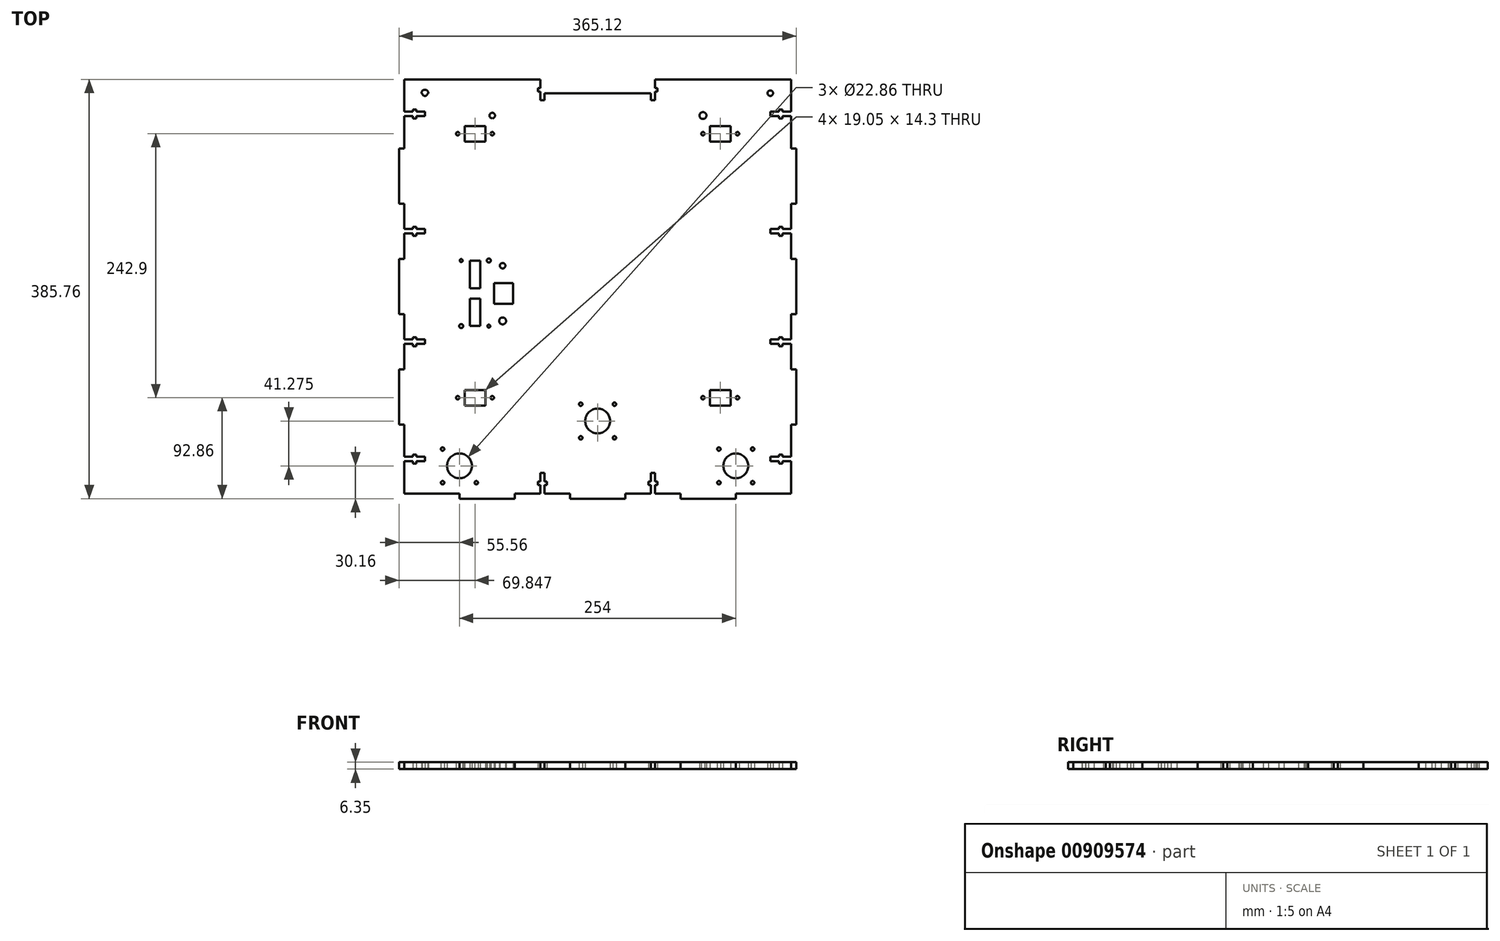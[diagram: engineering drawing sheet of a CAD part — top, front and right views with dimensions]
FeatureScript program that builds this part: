
annotation { "Feature Type Name" : "Feature", "Feature Type Description" : "" }
export const myFeature = defineFeature(function(context is Context, id is Id, definition is map)
    precondition{}
    {
        {
            var Q0;
            Q0=qCreatedBy(makeId("Top.planeOp"),FACE);
            var sketch = newSketch(context, id + "F0", { "sketchPlane" : qUnion([Q0])});
            skLineSegment(sketch, "E0.bottom", {"start": v(-177.8, 184.15) * mm, "end": v(177.8, 184.15) * mm});
            skLineSegment(sketch, "E0.top", {"start": v(-177.8, -184.15) * mm, "end": v(177.8, -184.15) * mm});
            skLineSegment(sketch, "E0.left", {"start": v(-177.8, 184.15) * mm, "end": v(-177.8, -184.15) * mm});
            skLineSegment(sketch, "E0.right", {"start": v(177.8, 184.15) * mm, "end": v(177.8, -184.15) * mm});
            skPoint(sketch, "E0.middle", {"position": v(0, 0) * mm});
            skLineSegment(sketch, "E1.0", {"start": v(-133.35, -88.9) * mm, "end": v(133.35, -88.9) * mm});
            skLineSegment(sketch, "E2.0", {"start": v(-133.35, 139.7) * mm, "end": v(-133.35, -88.9) * mm});
            skLineSegment(sketch, "E3", {"start": v(0, 184.15) * mm, "end": v(0, -184.15) * mm, "construction": true});
            skLineSegment(sketch, "E4", {"start": v(-177.8, 0) * mm, "end": v(177.8, 0) * mm, "construction": true});
            skLineSegment(sketch, "E5.MirrorCS", {"start": v(133.35, 139.7) * mm, "end": v(133.35, -88.9) * mm});
            skLineSegment(sketch, "E6.0", {"start": v(-133.35, 139.7) * mm, "end": v(133.35, 139.7) * mm});
            skLineSegment(sketch, "E7.bottom", {"start": v(-130.17, 34.93) * mm, "end": v(-95.25, 34.93) * mm});
            skLineSegment(sketch, "E7.top", {"start": v(-130.17, -34.92) * mm, "end": v(-95.25, -34.92) * mm});
            skLineSegment(sketch, "E7.left", {"start": v(-130.18, 34.92) * mm, "end": v(-130.18, -34.92) * mm});
            skLineSegment(sketch, "E7.right", {"start": v(-95.25, 34.92) * mm, "end": v(-95.25, -34.92) * mm});
            skLineSegment(sketch, "E8.bottom", {"start": v(-107.95, 4.76) * mm, "end": v(-117.48, 4.76) * mm});
            skLineSegment(sketch, "E8.top", {"start": v(-107.95, 30.04) * mm, "end": v(-117.48, 30.04) * mm});
            skLineSegment(sketch, "E8.left", {"start": v(-107.95, 4.76) * mm, "end": v(-107.95, 30.04) * mm});
            skLineSegment(sketch, "E8.right", {"start": v(-117.48, 4.76) * mm, "end": v(-117.48, 30.04) * mm});
            skPoint(sketch, "E9", {"position": v(-95.25, 0) * mm});
            skLineSegment(sketch, "E10.MirrorCS", {"start": v(-117.48, -4.76) * mm, "end": v(-117.48, -30.04) * mm});
            skLineSegment(sketch, "E11.MirrorCS", {"start": v(-107.95, -4.76) * mm, "end": v(-107.95, -30.04) * mm});
            skPoint(sketch, "E12.MirrorP", {"position": v(-112.71, -12.57) * mm});
            skLineSegment(sketch, "E13.MirrorCS", {"start": v(-107.95, -4.76) * mm, "end": v(-117.48, -4.76) * mm});
            skLineSegment(sketch, "E14.MirrorCS", {"start": v(-107.95, -30.04) * mm, "end": v(-117.48, -30.04) * mm});
            skCircle(sketch, "E15", {"center": v(-127, -158.75) * mm, "radius": 11.43 * mm});
            skCircle(sketch, "E16", {"center": v(-111.5, -143.26) * mm, "radius": 1.59 * mm});
            skCircle(sketch, "E17.1.0", {"center": v(-142.5, -143.26) * mm, "radius": 1.59 * mm});
            skCircle(sketch, "E17.2.0", {"center": v(-142.5, -174.24) * mm, "radius": 1.59 * mm});
            skCircle(sketch, "E17.3.0", {"center": v(-111.5, -174.24) * mm, "radius": 1.59 * mm});
            skCircle(sketch, "E18.MirrorC", {"center": v(142.5, -143.26) * mm, "radius": 1.59 * mm});
            skCircle(sketch, "E19.MirrorC", {"center": v(111.5, -143.26) * mm, "radius": 1.59 * mm});
            skCircle(sketch, "E20.MirrorC", {"center": v(142.5, -174.24) * mm, "radius": 1.59 * mm});
            skPoint(sketch, "E21.MirrorP", {"position": v(127, -158.75) * mm});
            skCircle(sketch, "E22.MirrorC", {"center": v(111.5, -174.24) * mm, "radius": 1.59 * mm});
            skCircle(sketch, "E23.MirrorC", {"center": v(127, -158.75) * mm, "radius": 11.43 * mm});
            skPoint(sketch, "E24.orphan", {"position": v(-112.71, -34.93) * mm});
            skCircle(sketch, "E25", {"center": v(-128.59, -96.05) * mm, "radius": 1.59 * mm});
            skCircle(sketch, "E26.MirrorC", {"center": v(-96.84, -96.05) * mm, "radius": 1.59 * mm});
            skLineSegment(sketch, "E27.bottom", {"start": v(-122.24, -88.9) * mm, "end": v(-103.19, -88.9) * mm});
            skLineSegment(sketch, "E27.top", {"start": v(-122.24, -103.2) * mm, "end": v(-103.19, -103.2) * mm});
            skLineSegment(sketch, "E27.left", {"start": v(-122.24, -88.9) * mm, "end": v(-122.24, -103.2) * mm});
            skLineSegment(sketch, "E27.right", {"start": v(-103.19, -88.9) * mm, "end": v(-103.19, -103.2) * mm});
            skPoint(sketch, "E28", {"position": v(-112.71, -103.2) * mm});
            skLineSegment(sketch, "E29.MirrorCS", {"start": v(122.24, -88.9) * mm, "end": v(122.24, -103.2) * mm});
            skCircle(sketch, "E30.MirrorC", {"center": v(96.84, -96.05) * mm, "radius": 1.59 * mm});
            skCircle(sketch, "E31.MirrorC", {"center": v(128.59, -96.05) * mm, "radius": 1.59 * mm});
            skLineSegment(sketch, "E32.MirrorCS", {"start": v(122.24, -88.9) * mm, "end": v(103.19, -88.9) * mm});
            skPoint(sketch, "E33.MirrorP", {"position": v(112.71, -103.2) * mm});
            skLineSegment(sketch, "E34.MirrorCS", {"start": v(103.19, -88.9) * mm, "end": v(103.19, -103.2) * mm});
            skLineSegment(sketch, "E35.MirrorCS", {"start": v(122.24, -103.2) * mm, "end": v(103.19, -103.2) * mm});
            skLineSegment(sketch, "E36.bottom", {"start": v(-95.25, -9.53) * mm, "end": v(-77.79, -9.53) * mm});
            skLineSegment(sketch, "E36.top", {"start": v(-95.25, 9.52) * mm, "end": v(-77.79, 9.52) * mm});
            skLineSegment(sketch, "E36.left", {"start": v(-95.25, -9.53) * mm, "end": v(-95.25, 9.52) * mm});
            skLineSegment(sketch, "E36.right", {"start": v(-77.79, -9.53) * mm, "end": v(-77.79, 9.52) * mm});
            skPoint(sketch, "E37", {"position": v(-65.09, 0) * mm});
            skLineSegment(sketch, "E38.bottom", {"start": v(-95.25, -34.92) * mm, "end": v(-77.79, -34.92) * mm});
            skLineSegment(sketch, "E38.top", {"start": v(-95.25, 34.93) * mm, "end": v(-77.79, 34.93) * mm});
            skLineSegment(sketch, "E38.left", {"start": v(-95.25, -34.92) * mm, "end": v(-95.25, 34.92) * mm});
            skLineSegment(sketch, "E38.right", {"start": v(-77.79, -34.92) * mm, "end": v(-77.79, 34.92) * mm});
            skLineSegment(sketch, "E39.0", {"start": v(-100.01, 34.92) * mm, "end": v(-77.79, 34.92) * mm});
            skLineSegment(sketch, "E39.1", {"start": v(-130.18, 34.92) * mm, "end": v(-100.01, 34.92) * mm});
            skLineSegment(sketch, "E40", {"start": v(-77.79, 34.92) * mm, "end": v(-77.79, 34.92) * mm});
            skLineSegment(sketch, "E41", {"start": v(-130.18, 34.92) * mm, "end": v(-130.18, 34.92) * mm});
            skLineSegment(sketch, "E42.MirrorCS", {"start": v(-130.18, -34.92) * mm, "end": v(-130.18, -34.92) * mm});
            skLineSegment(sketch, "E43.MirrorCS", {"start": v(-100.01, -34.93) * mm, "end": v(-77.79, -34.93) * mm});
            skLineSegment(sketch, "E44.MirrorCS", {"start": v(-130.18, -34.93) * mm, "end": v(-100.01, -34.93) * mm});
            skLineSegment(sketch, "E45.MirrorCS", {"start": v(-77.79, -34.92) * mm, "end": v(-77.79, -34.92) * mm});
            skCircle(sketch, "E46", {"center": v(-87.31, 25.4) * mm, "radius": 3.18 * mm});
            skCircle(sketch, "E47.MirrorC", {"center": v(-87.31, -25.4) * mm, "radius": 3.18 * mm});
            skCircle(sketch, "E48", {"center": v(-125.41, 30.16) * mm, "radius": 1.84 * mm});
            skCircle(sketch, "E49.MirrorC", {"center": v(-100.01, 30.16) * mm, "radius": 1.84 * mm});
            skCircle(sketch, "E50.MirrorC", {"center": v(-125.41, -30.16) * mm, "radius": 1.84 * mm});
            skCircle(sketch, "E51.MirrorC", {"center": v(-100.01, -30.16) * mm, "radius": 1.84 * mm});
            skCircle(sketch, "E52", {"center": v(-158.75, 184.15) * mm, "radius": 3.18 * mm});
            skCircle(sketch, "E53", {"center": v(-96.84, 163.55) * mm, "radius": 3.18 * mm});
            skCircle(sketch, "E54.MirrorC", {"center": v(158.75, 184.15) * mm, "radius": 3.18 * mm});
            skLineSegment(sketch, "E55.0", {"start": v(-177.8, 196.85) * mm, "end": v(177.8, 196.85) * mm});
            skLineSegment(sketch, "E56", {"start": v(-177.8, 184.15) * mm, "end": v(-177.8, 196.85) * mm});
            skLineSegment(sketch, "E57", {"start": v(177.8, 184.15) * mm, "end": v(177.8, 196.85) * mm});
            skLineSegment(sketch, "E58.bottom", {"start": v(-177.8, 133.35) * mm, "end": v(-182.56, 133.35) * mm});
            skLineSegment(sketch, "E58.top", {"start": v(-177.8, 82.55) * mm, "end": v(-182.56, 82.55) * mm});
            skLineSegment(sketch, "E58.left", {"start": v(-177.8, 133.35) * mm, "end": v(-177.8, 82.55) * mm});
            skLineSegment(sketch, "E58.right", {"start": v(-182.56, 133.35) * mm, "end": v(-182.56, 82.55) * mm});
            skLineSegment(sketch, "E59.bottom", {"start": v(-177.8, 31.75) * mm, "end": v(-182.56, 31.75) * mm});
            skLineSegment(sketch, "E59.top", {"start": v(-177.8, -19.05) * mm, "end": v(-182.56, -19.05) * mm});
            skLineSegment(sketch, "E59.left", {"start": v(-177.8, 31.75) * mm, "end": v(-177.8, -19.05) * mm});
            skLineSegment(sketch, "E59.right", {"start": v(-182.56, 31.75) * mm, "end": v(-182.56, -19.05) * mm});
            skLineSegment(sketch, "E60.bottom", {"start": v(-177.8, -69.85) * mm, "end": v(-182.56, -69.85) * mm});
            skLineSegment(sketch, "E60.top", {"start": v(-177.8, -120.65) * mm, "end": v(-182.56, -120.65) * mm});
            skLineSegment(sketch, "E60.left", {"start": v(-177.8, -69.85) * mm, "end": v(-177.8, -120.65) * mm});
            skLineSegment(sketch, "E60.right", {"start": v(-182.56, -69.85) * mm, "end": v(-182.56, -120.65) * mm});
            skLineSegment(sketch, "E61.MirrorCS", {"start": v(177.8, -120.65) * mm, "end": v(182.56, -120.65) * mm});
            skLineSegment(sketch, "E62.MirrorCS", {"start": v(177.8, 31.75) * mm, "end": v(182.56, 31.75) * mm});
            skLineSegment(sketch, "E63.MirrorCS", {"start": v(177.8, -19.05) * mm, "end": v(182.56, -19.05) * mm});
            skLineSegment(sketch, "E64.MirrorCS", {"start": v(177.8, 82.55) * mm, "end": v(182.56, 82.55) * mm});
            skLineSegment(sketch, "E65.MirrorCS", {"start": v(177.8, -69.85) * mm, "end": v(182.56, -69.85) * mm});
            skLineSegment(sketch, "E66.MirrorCS", {"start": v(177.8, 133.35) * mm, "end": v(182.56, 133.35) * mm});
            skLineSegment(sketch, "E67.MirrorCS", {"start": v(182.56, 133.35) * mm, "end": v(182.56, 82.55) * mm});
            skLineSegment(sketch, "E68.MirrorCS", {"start": v(177.8, 31.75) * mm, "end": v(177.8, -19.05) * mm});
            skLineSegment(sketch, "E69.MirrorCS", {"start": v(182.56, 31.75) * mm, "end": v(182.56, -19.05) * mm});
            skLineSegment(sketch, "E70.MirrorCS", {"start": v(177.8, 133.35) * mm, "end": v(177.8, 82.55) * mm});
            skLineSegment(sketch, "E71.MirrorCS", {"start": v(177.8, -69.85) * mm, "end": v(177.8, -120.65) * mm});
            skLineSegment(sketch, "E72.MirrorCS", {"start": v(182.56, -69.85) * mm, "end": v(182.56, -120.65) * mm});
            skLineSegment(sketch, "E73.bottom", {"start": v(-127, 196.85) * mm, "end": v(-76.2, 196.85) * mm});
            skLineSegment(sketch, "E73.top", {"start": v(-127, 201.61) * mm, "end": v(-76.2, 201.61) * mm});
            skLineSegment(sketch, "E73.left", {"start": v(-127, 196.85) * mm, "end": v(-127, 201.61) * mm});
            skLineSegment(sketch, "E73.right", {"start": v(-76.2, 196.85) * mm, "end": v(-76.2, 201.61) * mm});
            skLineSegment(sketch, "E74.bottom", {"start": v(-25.4, 196.85) * mm, "end": v(25.4, 196.85) * mm});
            skLineSegment(sketch, "E74.top", {"start": v(-25.4, 201.61) * mm, "end": v(25.4, 201.61) * mm});
            skLineSegment(sketch, "E74.left", {"start": v(-25.4, 196.85) * mm, "end": v(-25.4, 201.61) * mm});
            skLineSegment(sketch, "E74.right", {"start": v(25.4, 196.85) * mm, "end": v(25.4, 201.61) * mm});
            skLineSegment(sketch, "E75.bottom", {"start": v(76.2, 196.85) * mm, "end": v(127, 196.85) * mm});
            skLineSegment(sketch, "E75.top", {"start": v(76.2, 201.61) * mm, "end": v(127, 201.61) * mm});
            skLineSegment(sketch, "E75.left", {"start": v(76.2, 196.85) * mm, "end": v(76.2, 201.61) * mm});
            skLineSegment(sketch, "E75.right", {"start": v(127, 196.85) * mm, "end": v(127, 201.61) * mm});
            skLineSegment(sketch, "E76", {"start": v(177.8, 196.85) * mm, "end": v(177.8, -184.15) * mm, "construction": true});
            skLineSegment(sketch, "E77", {"start": v(177.8, 6.35) * mm, "end": v(-210.69, 6.35) * mm, "construction": true});
            skLineSegment(sketch, "E78.MirrorCS", {"start": v(25.4, -184.15) * mm, "end": v(25.4, -188.91) * mm});
            skLineSegment(sketch, "E79.MirrorCS", {"start": v(76.2, -184.15) * mm, "end": v(76.2, -188.91) * mm});
            skLineSegment(sketch, "E80.MirrorCS", {"start": v(127, -184.15) * mm, "end": v(127, -188.91) * mm});
            skLineSegment(sketch, "E81.MirrorCS", {"start": v(-127, -184.15) * mm, "end": v(-127, -188.91) * mm});
            skLineSegment(sketch, "E82.MirrorCS", {"start": v(-25.4, -184.15) * mm, "end": v(-25.4, -188.91) * mm});
            skLineSegment(sketch, "E83.MirrorCS", {"start": v(-76.2, -184.15) * mm, "end": v(-76.2, -188.91) * mm});
            skLineSegment(sketch, "E84.MirrorCS", {"start": v(76.2, -184.15) * mm, "end": v(127, -184.15) * mm});
            skLineSegment(sketch, "E85.MirrorCS", {"start": v(-127, -188.91) * mm, "end": v(-76.2, -188.91) * mm});
            skLineSegment(sketch, "E86.MirrorCS", {"start": v(76.2, -188.91) * mm, "end": v(127, -188.91) * mm});
            skLineSegment(sketch, "E87.MirrorCS", {"start": v(-25.4, -184.15) * mm, "end": v(25.4, -184.15) * mm});
            skLineSegment(sketch, "E88.MirrorCS", {"start": v(-25.4, -188.91) * mm, "end": v(25.4, -188.91) * mm});
            skLineSegment(sketch, "E89.MirrorCS", {"start": v(-127, -184.15) * mm, "end": v(-76.2, -184.15) * mm});
            skCircle(sketch, "E90", {"center": v(0, -117.47) * mm, "radius": 11.43 * mm});
            skLineSegment(sketch, "E91.bottom", {"start": v(20.64, -96.84) * mm, "end": v(-20.64, -96.84) * mm});
            skLineSegment(sketch, "E91.top", {"start": v(20.64, -138.11) * mm, "end": v(-20.64, -138.11) * mm});
            skLineSegment(sketch, "E91.left", {"start": v(20.64, -96.84) * mm, "end": v(20.64, -138.11) * mm});
            skLineSegment(sketch, "E91.right", {"start": v(-20.64, -96.84) * mm, "end": v(-20.64, -138.11) * mm});
            skCircle(sketch, "E92", {"center": v(-15.5, -132.97) * mm, "radius": 1.59 * mm});
            skCircle(sketch, "E93.1.0", {"center": v(15.5, -132.97) * mm, "radius": 1.59 * mm});
            skCircle(sketch, "E93.2.0", {"center": v(15.5, -101.98) * mm, "radius": 1.59 * mm});
            skCircle(sketch, "E94.1.3.0", {"center": v(-15.5, -101.98) * mm, "radius": 1.59 * mm});
            skPoint(sketch, "E95.orphan", {"position": v(-112.71, 34.93) * mm});
            skLineSegment(sketch, "E96", {"start": v(133.35, 25.4) * mm, "end": v(-130.18, 25.4) * mm, "construction": true});
            skCircle(sketch, "E97.MirrorC", {"center": v(-128.59, 146.85) * mm, "radius": 1.59 * mm});
            skLineSegment(sketch, "E98.MirrorCS", {"start": v(-122.24, 154) * mm, "end": v(-103.19, 154) * mm});
            skCircle(sketch, "E99.MirrorC", {"center": v(-96.84, 146.85) * mm, "radius": 1.59 * mm});
            skLineSegment(sketch, "E100.MirrorCS", {"start": v(-122.24, 139.7) * mm, "end": v(-103.19, 139.7) * mm});
            skLineSegment(sketch, "E101.MirrorCS", {"start": v(-122.24, 139.7) * mm, "end": v(-122.24, 154) * mm});
            skLineSegment(sketch, "E102.MirrorCS", {"start": v(-103.19, 139.7) * mm, "end": v(-103.19, 154) * mm});
            skPoint(sketch, "E103.MirrorP", {"position": v(-112.71, 154) * mm});
            skCircle(sketch, "E104.MirrorC", {"center": v(96.84, 146.85) * mm, "radius": 1.59 * mm});
            skLineSegment(sketch, "E105.MirrorCS", {"start": v(122.24, 154) * mm, "end": v(103.19, 154) * mm});
            skCircle(sketch, "E106.MirrorC", {"center": v(128.59, 146.85) * mm, "radius": 1.59 * mm});
            skLineSegment(sketch, "E107.MirrorCS", {"start": v(122.24, 139.7) * mm, "end": v(103.19, 139.7) * mm});
            skLineSegment(sketch, "E108.MirrorCS", {"start": v(103.19, 139.7) * mm, "end": v(103.19, 154) * mm});
            skPoint(sketch, "E109.MirrorP", {"position": v(112.71, 154) * mm});
            skLineSegment(sketch, "E110.MirrorCS", {"start": v(122.24, 139.7) * mm, "end": v(122.24, 154) * mm});
            skCircle(sketch, "E111.MirrorC", {"center": v(96.84, 163.55) * mm, "radius": 3.18 * mm});
            skLineSegment(sketch, "E112.bottom", {"start": v(-158.75, -150.4) * mm, "end": v(-158.75, -154.4) * mm});
            skLineSegment(sketch, "E112.top", {"start": v(-177.8, -150.4) * mm, "end": v(-177.8, -154.4) * mm});
            skLineSegment(sketch, "E112.left", {"start": v(-158.75, -150.4) * mm, "end": v(-177.8, -150.4) * mm});
            skLineSegment(sketch, "E112.right", {"start": v(-158.75, -154.4) * mm, "end": v(-177.8, -154.4) * mm});
            skPoint(sketch, "E113", {"position": v(-177.8, -152.4) * mm});
            skLineSegment(sketch, "E114.bottom", {"start": v(-166.67, -148.27) * mm, "end": v(-166.67, -156.53) * mm});
            skLineSegment(sketch, "E114.top", {"start": v(-169.85, -148.27) * mm, "end": v(-169.85, -156.53) * mm});
            skLineSegment(sketch, "E114.left", {"start": v(-166.67, -148.27) * mm, "end": v(-169.85, -148.27) * mm});
            skLineSegment(sketch, "E114.right", {"start": v(-166.67, -156.53) * mm, "end": v(-169.85, -156.53) * mm});
            skPoint(sketch, "E115", {"position": v(-169.85, -152.4) * mm});
            skLineSegment(sketch, "E116", {"start": v(-177.8, -19.05) * mm, "end": v(-177.8, -69.85) * mm, "construction": true});
            skLineSegment(sketch, "E117", {"start": v(-177.8, -120.65) * mm, "end": v(-177.8, -184.15) * mm, "construction": true});
            skLineSegment(sketch, "E118", {"start": v(-177.8, 31.75) * mm, "end": v(-177.8, 82.55) * mm, "construction": true});
            skLineSegment(sketch, "E119", {"start": v(-177.8, 133.35) * mm, "end": v(-177.8, 196.85) * mm, "construction": true});
            skPoint(sketch, "E120", {"position": v(-177.8, 165.1) * mm});
            skPoint(sketch, "E121", {"position": v(-177.8, 57.15) * mm});
            skPoint(sketch, "E122", {"position": v(-177.8, -44.45) * mm});
            skLineSegment(sketch, "E123.bottom", {"start": v(-158.75, -42.46) * mm, "end": v(-158.75, -46.44) * mm});
            skLineSegment(sketch, "E123.top", {"start": v(-177.8, -42.46) * mm, "end": v(-177.8, -46.44) * mm});
            skLineSegment(sketch, "E123.left", {"start": v(-158.75, -42.46) * mm, "end": v(-177.8, -42.46) * mm});
            skLineSegment(sketch, "E123.right", {"start": v(-158.75, -46.44) * mm, "end": v(-177.8, -46.44) * mm});
            skLineSegment(sketch, "E124.bottom", {"start": v(-166.67, -40.32) * mm, "end": v(-166.67, -48.58) * mm});
            skLineSegment(sketch, "E124.top", {"start": v(-169.85, -40.32) * mm, "end": v(-169.85, -48.58) * mm});
            skLineSegment(sketch, "E124.left", {"start": v(-166.67, -40.32) * mm, "end": v(-169.85, -40.32) * mm});
            skLineSegment(sketch, "E124.right", {"start": v(-166.67, -48.58) * mm, "end": v(-169.85, -48.58) * mm});
            skPoint(sketch, "E125", {"position": v(-169.85, -44.45) * mm});
            skLineSegment(sketch, "E126.bottom", {"start": v(-158.75, 59.14) * mm, "end": v(-158.75, 55.16) * mm});
            skLineSegment(sketch, "E126.top", {"start": v(-177.8, 59.14) * mm, "end": v(-177.8, 55.16) * mm});
            skLineSegment(sketch, "E126.left", {"start": v(-158.75, 59.14) * mm, "end": v(-177.8, 59.14) * mm});
            skLineSegment(sketch, "E126.right", {"start": v(-158.75, 55.16) * mm, "end": v(-177.8, 55.16) * mm});
            skLineSegment(sketch, "E127.bottom", {"start": v(-166.67, 61.28) * mm, "end": v(-166.67, 53.02) * mm});
            skLineSegment(sketch, "E127.top", {"start": v(-169.85, 61.28) * mm, "end": v(-169.85, 53.02) * mm});
            skLineSegment(sketch, "E127.left", {"start": v(-166.67, 61.28) * mm, "end": v(-169.85, 61.28) * mm});
            skLineSegment(sketch, "E127.right", {"start": v(-166.67, 53.02) * mm, "end": v(-169.85, 53.02) * mm});
            skPoint(sketch, "E128", {"position": v(-169.85, 57.15) * mm});
            skLineSegment(sketch, "E129.bottom", {"start": v(-158.75, 167.1) * mm, "end": v(-158.75, 163.1) * mm});
            skLineSegment(sketch, "E129.top", {"start": v(-177.8, 167.1) * mm, "end": v(-177.8, 163.1) * mm});
            skLineSegment(sketch, "E129.left", {"start": v(-158.75, 167.1) * mm, "end": v(-177.8, 167.1) * mm});
            skLineSegment(sketch, "E129.right", {"start": v(-158.75, 163.1) * mm, "end": v(-177.8, 163.1) * mm});
            skLineSegment(sketch, "E130.bottom", {"start": v(-166.67, 169.23) * mm, "end": v(-166.67, 160.97) * mm});
            skLineSegment(sketch, "E130.top", {"start": v(-169.85, 169.23) * mm, "end": v(-169.85, 160.97) * mm});
            skLineSegment(sketch, "E130.left", {"start": v(-166.67, 169.23) * mm, "end": v(-169.85, 169.23) * mm});
            skLineSegment(sketch, "E130.right", {"start": v(-166.67, 160.97) * mm, "end": v(-169.85, 160.97) * mm});
            skPoint(sketch, "E131", {"position": v(-169.85, 165.1) * mm});
            skLineSegment(sketch, "E132.MirrorCS", {"start": v(177.8, 167.1) * mm, "end": v(177.8, 163.1) * mm});
            skLineSegment(sketch, "E133.MirrorCS", {"start": v(166.67, 169.23) * mm, "end": v(169.85, 169.23) * mm});
            skPoint(sketch, "E134.MirrorP", {"position": v(177.8, 165.1) * mm});
            skLineSegment(sketch, "E135.MirrorCS", {"start": v(158.75, 163.1) * mm, "end": v(177.8, 163.1) * mm});
            skLineSegment(sketch, "E136.MirrorCS", {"start": v(169.85, 169.23) * mm, "end": v(169.85, 160.97) * mm});
            skPoint(sketch, "E137.MirrorP", {"position": v(169.85, 165.1) * mm});
            skLineSegment(sketch, "E138.MirrorCS", {"start": v(166.67, 169.23) * mm, "end": v(166.67, 160.97) * mm});
            skLineSegment(sketch, "E139.MirrorCS", {"start": v(158.75, 167.1) * mm, "end": v(158.75, 163.1) * mm});
            skLineSegment(sketch, "E140.MirrorCS", {"start": v(158.75, 167.1) * mm, "end": v(177.8, 167.1) * mm});
            skLineSegment(sketch, "E141.MirrorCS", {"start": v(166.67, 160.97) * mm, "end": v(169.85, 160.97) * mm});
            skLineSegment(sketch, "E142.MirrorCS", {"start": v(177.8, 59.14) * mm, "end": v(177.8, 55.16) * mm});
            skLineSegment(sketch, "E143.MirrorCS", {"start": v(166.67, 61.28) * mm, "end": v(169.85, 61.28) * mm});
            skPoint(sketch, "E144.MirrorP", {"position": v(177.8, 57.15) * mm});
            skLineSegment(sketch, "E145.MirrorCS", {"start": v(158.75, 59.14) * mm, "end": v(177.8, 59.14) * mm});
            skLineSegment(sketch, "E146.MirrorCS", {"start": v(166.67, 61.28) * mm, "end": v(166.67, 53.02) * mm});
            skLineSegment(sketch, "E147.MirrorCS", {"start": v(169.85, 61.28) * mm, "end": v(169.85, 53.02) * mm});
            skLineSegment(sketch, "E148.MirrorCS", {"start": v(166.67, 53.02) * mm, "end": v(169.85, 53.02) * mm});
            skPoint(sketch, "E149.MirrorP", {"position": v(169.85, 57.15) * mm});
            skLineSegment(sketch, "E150.MirrorCS", {"start": v(158.75, 55.16) * mm, "end": v(177.8, 55.16) * mm});
            skLineSegment(sketch, "E151.MirrorCS", {"start": v(158.75, 59.14) * mm, "end": v(158.75, 55.16) * mm});
            skLineSegment(sketch, "E152.MirrorCS", {"start": v(177.8, -42.46) * mm, "end": v(177.8, -46.44) * mm});
            skLineSegment(sketch, "E153.MirrorCS", {"start": v(166.67, -40.32) * mm, "end": v(169.85, -40.32) * mm});
            skPoint(sketch, "E154.MirrorP", {"position": v(177.8, -44.45) * mm});
            skLineSegment(sketch, "E155.MirrorCS", {"start": v(169.85, -40.32) * mm, "end": v(169.85, -48.58) * mm});
            skPoint(sketch, "E156.MirrorP", {"position": v(169.85, -44.45) * mm});
            skLineSegment(sketch, "E157.MirrorCS", {"start": v(158.75, -42.46) * mm, "end": v(158.75, -46.44) * mm});
            skLineSegment(sketch, "E158.MirrorCS", {"start": v(166.67, -40.32) * mm, "end": v(166.67, -48.58) * mm});
            skLineSegment(sketch, "E159.MirrorCS", {"start": v(166.67, -48.58) * mm, "end": v(169.85, -48.58) * mm});
            skLineSegment(sketch, "E160.MirrorCS", {"start": v(158.75, -42.46) * mm, "end": v(177.8, -42.46) * mm});
            skLineSegment(sketch, "E161.MirrorCS", {"start": v(158.75, -46.44) * mm, "end": v(177.8, -46.44) * mm});
            skLineSegment(sketch, "E162.MirrorCS", {"start": v(177.8, -150.4) * mm, "end": v(177.8, -154.4) * mm});
            skLineSegment(sketch, "E163.MirrorCS", {"start": v(166.67, -148.27) * mm, "end": v(169.85, -148.27) * mm});
            skPoint(sketch, "E164.MirrorP", {"position": v(177.8, -152.4) * mm});
            skLineSegment(sketch, "E165.MirrorCS", {"start": v(158.75, -150.4) * mm, "end": v(158.75, -154.4) * mm});
            skLineSegment(sketch, "E166.MirrorCS", {"start": v(166.67, -148.27) * mm, "end": v(166.67, -156.53) * mm});
            skLineSegment(sketch, "E167.MirrorCS", {"start": v(166.67, -156.53) * mm, "end": v(169.85, -156.53) * mm});
            skLineSegment(sketch, "E168.MirrorCS", {"start": v(158.75, -150.4) * mm, "end": v(177.8, -150.4) * mm});
            skLineSegment(sketch, "E169.MirrorCS", {"start": v(169.85, -148.27) * mm, "end": v(169.85, -156.53) * mm});
            skPoint(sketch, "E170.MirrorP", {"position": v(169.85, -152.4) * mm});
            skLineSegment(sketch, "E171.MirrorCS", {"start": v(158.75, -154.4) * mm, "end": v(177.8, -154.4) * mm});
            skLineSegment(sketch, "E172", {"start": v(-76.2, 196.85) * mm, "end": v(-25.4, 196.85) * mm, "construction": true});
            skLineSegment(sketch, "E173", {"start": v(25.4, 196.85) * mm, "end": v(76.2, 196.85) * mm, "construction": true});
            skLineSegment(sketch, "E174", {"start": v(-76.2, -184.15) * mm, "end": v(-25.4, -184.15) * mm, "construction": true});
            skLineSegment(sketch, "E175", {"start": v(25.4, -184.15) * mm, "end": v(76.2, -184.15) * mm, "construction": true});
            skLineSegment(sketch, "E176.bottom", {"start": v(-48.8, 177.8) * mm, "end": v(-52.8, 177.8) * mm});
            skLineSegment(sketch, "E176.top", {"start": v(-48.8, 196.85) * mm, "end": v(-52.8, 196.85) * mm});
            skLineSegment(sketch, "E176.left", {"start": v(-48.8, 177.8) * mm, "end": v(-48.8, 196.85) * mm});
            skLineSegment(sketch, "E176.right", {"start": v(-52.8, 177.8) * mm, "end": v(-52.8, 196.85) * mm});
            skPoint(sketch, "E177", {"position": v(-50.8, 196.85) * mm});
            skLineSegment(sketch, "E178.bottom", {"start": v(-46.67, 185.72) * mm, "end": v(-54.93, 185.72) * mm});
            skLineSegment(sketch, "E178.top", {"start": v(-46.67, 188.9) * mm, "end": v(-54.93, 188.9) * mm});
            skLineSegment(sketch, "E178.left", {"start": v(-46.67, 185.72) * mm, "end": v(-46.67, 188.9) * mm});
            skLineSegment(sketch, "E178.right", {"start": v(-54.93, 185.72) * mm, "end": v(-54.93, 188.9) * mm});
            skPoint(sketch, "E179", {"position": v(-50.8, 188.9) * mm});
            skPoint(sketch, "E180", {"position": v(50.8, 196.85) * mm});
            skLineSegment(sketch, "E181.bottom", {"start": v(52.8, 177.8) * mm, "end": v(48.8, 177.8) * mm});
            skLineSegment(sketch, "E181.top", {"start": v(52.8, 196.85) * mm, "end": v(48.8, 196.85) * mm});
            skLineSegment(sketch, "E181.left", {"start": v(52.8, 177.8) * mm, "end": v(52.8, 196.85) * mm});
            skLineSegment(sketch, "E181.right", {"start": v(48.8, 177.8) * mm, "end": v(48.8, 196.85) * mm});
            skLineSegment(sketch, "E182.bottom", {"start": v(54.93, 185.72) * mm, "end": v(46.67, 185.72) * mm});
            skLineSegment(sketch, "E182.top", {"start": v(54.93, 188.9) * mm, "end": v(46.67, 188.9) * mm});
            skLineSegment(sketch, "E182.left", {"start": v(54.93, 185.72) * mm, "end": v(54.93, 188.9) * mm});
            skLineSegment(sketch, "E182.right", {"start": v(46.67, 185.72) * mm, "end": v(46.67, 188.9) * mm});
            skPoint(sketch, "E183", {"position": v(50.8, 188.9) * mm});
            skLineSegment(sketch, "E184.MirrorCS", {"start": v(-46.67, -173.02) * mm, "end": v(-46.67, -176.2) * mm});
            skLineSegment(sketch, "E185.MirrorCS", {"start": v(-48.8, -165.1) * mm, "end": v(-52.8, -165.1) * mm});
            skLineSegment(sketch, "E186.MirrorCS", {"start": v(-48.8, -184.15) * mm, "end": v(-52.8, -184.15) * mm});
            skLineSegment(sketch, "E187.MirrorCS", {"start": v(-54.93, -173.02) * mm, "end": v(-54.93, -176.2) * mm});
            skLineSegment(sketch, "E188.MirrorCS", {"start": v(-46.67, -173.02) * mm, "end": v(-54.93, -173.02) * mm});
            skLineSegment(sketch, "E189.MirrorCS", {"start": v(-46.67, -176.2) * mm, "end": v(-54.93, -176.2) * mm});
            skPoint(sketch, "E190.MirrorP", {"position": v(-50.8, -184.15) * mm});
            skLineSegment(sketch, "E191.MirrorCS", {"start": v(-48.8, -165.1) * mm, "end": v(-48.8, -184.15) * mm});
            skLineSegment(sketch, "E192.MirrorCS", {"start": v(-52.8, -165.1) * mm, "end": v(-52.8, -184.15) * mm});
            skPoint(sketch, "E193.MirrorP", {"position": v(-50.8, -176.2) * mm});
            skLineSegment(sketch, "E194.MirrorCS", {"start": v(54.93, -173.02) * mm, "end": v(54.93, -176.2) * mm});
            skLineSegment(sketch, "E195.MirrorCS", {"start": v(52.8, -184.15) * mm, "end": v(48.8, -184.15) * mm});
            skLineSegment(sketch, "E196.MirrorCS", {"start": v(46.67, -173.02) * mm, "end": v(46.67, -176.2) * mm});
            skLineSegment(sketch, "E197.MirrorCS", {"start": v(52.8, -165.1) * mm, "end": v(48.8, -165.1) * mm});
            skPoint(sketch, "E198.MirrorP", {"position": v(50.8, -184.15) * mm});
            skLineSegment(sketch, "E199.MirrorCS", {"start": v(54.93, -176.2) * mm, "end": v(46.67, -176.2) * mm});
            skLineSegment(sketch, "E200.MirrorCS", {"start": v(52.8, -165.1) * mm, "end": v(52.8, -184.15) * mm});
            skPoint(sketch, "E201.MirrorP", {"position": v(50.8, -176.2) * mm});
            skLineSegment(sketch, "E202.MirrorCS", {"start": v(48.8, -165.1) * mm, "end": v(48.8, -184.15) * mm});
            skLineSegment(sketch, "E203.MirrorCS", {"start": v(54.93, -173.02) * mm, "end": v(46.67, -173.02) * mm});
            skSolve(sketch);
        }
        {
            var Q0;
            Q0=makeQuery(id+"F0.imprint","IMPRINT",FACE,{"disambiguationData":[TD([[makeQuery(id+"F0.imprint","IMPRINT",EDGE,{"derivedFrom":sQuery(id+"F0.wireOp",EDGE,"E0.bottom")}),-1.0]])]});
            var Q1;
            {var subQ0=sQuery(id+"F0.wireOp",EDGE,"E7.bottom");Q1=makeQuery(id+"F0.imprint","IMPRINT",FACE,{"disambiguationData":[TD([[makeQuery(id+"F0.imprint","IMPRINT",EDGE,{"derivedFrom":subQ0}),-1.0]])]});}
            var Q2;
            {var subQ1=sQuery(id+"F0.wireOp",EDGE,"E36.bottom");Q2=makeQuery(id+"F0.imprint","IMPRINT",FACE,{"disambiguationData":[TD([[makeQuery(id+"F0.imprint","IMPRINT",EDGE,{"derivedFrom":subQ1}),-1.0]])]});}
            var Q3;
            {var subQ7=sQuery(id+"F0.wireOp",EDGE,"E36.top");Q3=makeQuery(id+"F0.imprint","IMPRINT",FACE,{"disambiguationData":[TD([[makeQuery(id+"F0.imprint","IMPRINT",EDGE,{"derivedFrom":subQ7}),1.0]])]});}
            var Q4;
            {var subQ0=sQuery(id+"F0.wireOp",EDGE,"E7.top");Q4=makeQuery(id+"F0.imprint","IMPRINT",FACE,{"disambiguationData":[TD([[makeQuery(id+"F0.imprint","IMPRINT",EDGE,{"derivedFrom":subQ0}),-1.0]])]});}
            var Q5;
            {var subQ1=sQuery(id+"F0.wireOp",EDGE,"E7.bottom");Q5=makeQuery(id+"F0.imprint","IMPRINT",FACE,{"disambiguationData":[TD([[makeQuery(id+"F0.imprint","IMPRINT",EDGE,{"derivedFrom":subQ1}),1.0]])]});}
            var Q6;
            {var subQ0=sQuery(id+"F0.wireOp",EDGE,"E46");var subQ1=sQuery(id+"F0.wireOp",EDGE,"E38.top");var subQ2=makeQuery(id+"F0.imprint","INTERSECT",VERTEX,{"disambiguationData":[OD(0.0)],"derivedFrom":[subQ1,subQ0]});Q6=makeQuery(id+"F0.imprint","IMPRINT",FACE,{"disambiguationData":[TD([[makeQuery(id+"F0.imprint","IMPRINT",EDGE,{"disambiguationData":[TD([[subQ2,-1.0]])],"derivedFrom":subQ1}),-1.0]])]});}
            var Q7;
            Q7=makeQuery(id+"F0.imprint","IMPRINT",FACE,{"disambiguationData":[TD([[makeQuery(id+"F0.imprint","IMPRINT",EDGE,{"derivedFrom":sQuery(id+"F0.wireOp",EDGE,"E49.MirrorC")}),-1.0]])]});
            var Q8;
            Q8=makeQuery(id+"F0.imprint","IMPRINT",FACE,{"disambiguationData":[TD([[makeQuery(id+"F0.imprint","IMPRINT",EDGE,{"derivedFrom":sQuery(id+"F0.wireOp",EDGE,"E48")}),1.0]])]});
            var Q9;
            Q9=makeQuery(id+"F0.imprint","IMPRINT",FACE,{"disambiguationData":[TD([[makeQuery(id+"F0.imprint","IMPRINT",EDGE,{"derivedFrom":sQuery(id+"F0.wireOp",EDGE,"E50.MirrorC")}),-1.0]])]});
            var Q10;
            {var subQ0=sQuery(id+"F0.wireOp",EDGE,"E46");var subQ1=sQuery(id+"F0.wireOp",EDGE,"E38.top");var subQ2=makeQuery(id+"F0.imprint","INTERSECT",VERTEX,{"disambiguationData":[OD(0.0)],"derivedFrom":[subQ1,subQ0]});Q10=makeQuery(id+"F0.imprint","IMPRINT",FACE,{"disambiguationData":[TD([[makeQuery(id+"F0.imprint","IMPRINT",EDGE,{"disambiguationData":[TD([[subQ2,-1.0]])],"derivedFrom":subQ1}),1.0]])]});}
            var Q11;
            Q11=makeQuery(id+"F0.imprint","IMPRINT",FACE,{"disambiguationData":[TD([[makeQuery(id+"F0.imprint","IMPRINT",EDGE,{"derivedFrom":sQuery(id+"F0.wireOp",EDGE,"E51.MirrorC")}),1.0]])]});
            var Q12;
            {var subQ0=sQuery(id+"F0.wireOp",EDGE,"E47.MirrorC");var subQ1=sQuery(id+"F0.wireOp",EDGE,"E38.bottom");var subQ2=makeQuery(id+"F0.imprint","INTERSECT",VERTEX,{"disambiguationData":[OD(0.0)],"derivedFrom":[subQ1,subQ0]});Q12=makeQuery(id+"F0.imprint","IMPRINT",FACE,{"disambiguationData":[TD([[makeQuery(id+"F0.imprint","IMPRINT",EDGE,{"disambiguationData":[TD([[subQ2,-1.0]])],"derivedFrom":subQ1}),1.0]])]});}
            var Q13;
            Q13=makeQuery(id+"F0.imprint","IMPRINT",FACE,{"disambiguationData":[TD([[makeQuery(id+"F0.imprint","IMPRINT",EDGE,{"derivedFrom":sQuery(id+"F0.wireOp",EDGE,"E0.top")}),1.0]])]});
            var Q14;
            Q14=makeQuery(id+"F0.imprint","IMPRINT",FACE,{"disambiguationData":[TD([[makeQuery(id+"F0.imprint","IMPRINT",EDGE,{"derivedFrom":sQuery(id+"F0.wireOp",EDGE,"E55.0")}),-1.0]])]});
            var Q15;
            {var subQ0=sQuery(id+"F0.wireOp",EDGE,"E52");var subQ1=sQuery(id+"F0.wireOp",EDGE,"E0.bottom");var subQ2=makeQuery(id+"F0.imprint","INTERSECT",VERTEX,{"disambiguationData":[OD(0.0)],"derivedFrom":[subQ1,subQ0]});Q15=makeQuery(id+"F0.imprint","IMPRINT",FACE,{"disambiguationData":[TD([[makeQuery(id+"F0.imprint","IMPRINT",EDGE,{"disambiguationData":[TD([[subQ2,-1.0]])],"derivedFrom":subQ1}),1.0]])]});}
            var Q16;
            {var subQ0=sQuery(id+"F0.wireOp",EDGE,"E54.MirrorC");var subQ1=sQuery(id+"F0.wireOp",EDGE,"E0.bottom");var subQ2=makeQuery(id+"F0.imprint","INTERSECT",VERTEX,{"disambiguationData":[OD(0.0)],"derivedFrom":[subQ1,subQ0]});Q16=makeQuery(id+"F0.imprint","IMPRINT",FACE,{"disambiguationData":[TD([[makeQuery(id+"F0.imprint","IMPRINT",EDGE,{"disambiguationData":[TD([[subQ2,-1.0]])],"derivedFrom":subQ1}),1.0]])]});}
            var Q17;
            Q17=makeQuery(id+"F0.imprint","IMPRINT",FACE,{"disambiguationData":[TD([[makeQuery(id+"F0.imprint","IMPRINT",EDGE,{"derivedFrom":sQuery(id+"F0.wireOp",EDGE,"E53")}),1.0]])]});
            var Q18;
            Q18=makeQuery(id+"F0.imprint","IMPRINT",FACE,{"disambiguationData":[TD([[makeQuery(id+"F0.imprint","IMPRINT",EDGE,{"derivedFrom":sQuery(id+"F0.wireOp",EDGE,"fdd06f5c-8cbb-4d59-a9f2-426be867a0200.MirrorC")}),-1.0]])]});
            var Q19;
            Q19=makeQuery(id+"F0.imprint","IMPRINT",FACE,{"disambiguationData":[TD([[makeQuery(id+"F0.imprint","IMPRINT",EDGE,{"derivedFrom":sQuery(id+"F0.wireOp",EDGE,"E58.bottom")}),1.0]])]});
            var Q20;
            Q20=makeQuery(id+"F0.imprint","IMPRINT",FACE,{"disambiguationData":[TD([[makeQuery(id+"F0.imprint","IMPRINT",EDGE,{"derivedFrom":sQuery(id+"F0.wireOp",EDGE,"E73.bottom")}),1.0]])]});
            var Q21;
            Q21=makeQuery(id+"F0.imprint","IMPRINT",FACE,{"disambiguationData":[TD([[makeQuery(id+"F0.imprint","IMPRINT",EDGE,{"derivedFrom":sQuery(id+"F0.wireOp",EDGE,"E74.bottom")}),1.0]])]});
            var Q22;
            Q22=makeQuery(id+"F0.imprint","IMPRINT",FACE,{"disambiguationData":[TD([[makeQuery(id+"F0.imprint","IMPRINT",EDGE,{"derivedFrom":sQuery(id+"F0.wireOp",EDGE,"E75.bottom")}),1.0]])]});
            var Q23;
            Q23=makeQuery(id+"F0.imprint","IMPRINT",FACE,{"disambiguationData":[TD([[makeQuery(id+"F0.imprint","IMPRINT",EDGE,{"derivedFrom":sQuery(id+"F0.wireOp",EDGE,"E64.MirrorCS")}),1.0]])]});
            var Q24;
            Q24=makeQuery(id+"F0.imprint","IMPRINT",FACE,{"disambiguationData":[TD([[makeQuery(id+"F0.imprint","IMPRINT",EDGE,{"derivedFrom":sQuery(id+"F0.wireOp",EDGE,"E62.MirrorCS")}),-1.0]])]});
            var Q25;
            Q25=makeQuery(id+"F0.imprint","IMPRINT",FACE,{"disambiguationData":[TD([[makeQuery(id+"F0.imprint","IMPRINT",EDGE,{"derivedFrom":sQuery(id+"F0.wireOp",EDGE,"E61.MirrorCS")}),1.0]])]});
            var Q26;
            Q26=makeQuery(id+"F0.imprint","IMPRINT",FACE,{"disambiguationData":[TD([[makeQuery(id+"F0.imprint","IMPRINT",EDGE,{"derivedFrom":sQuery(id+"F0.wireOp",EDGE,"E60.bottom")}),1.0]])]});
            var Q27;
            Q27=makeQuery(id+"F0.imprint","IMPRINT",FACE,{"disambiguationData":[TD([[makeQuery(id+"F0.imprint","IMPRINT",EDGE,{"derivedFrom":sQuery(id+"F0.wireOp",EDGE,"E59.bottom")}),1.0]])]});
            var Q28;
            Q28=makeQuery(id+"F0.imprint","IMPRINT",FACE,{"disambiguationData":[TD([[makeQuery(id+"F0.imprint","IMPRINT",EDGE,{"derivedFrom":sQuery(id+"F0.wireOp",EDGE,"E81.MirrorCS")}),1.0]])]});
            var Q29;
            Q29=makeQuery(id+"F0.imprint","IMPRINT",FACE,{"disambiguationData":[TD([[makeQuery(id+"F0.imprint","IMPRINT",EDGE,{"derivedFrom":sQuery(id+"F0.wireOp",EDGE,"E78.MirrorCS")}),-1.0]])]});
            var Q30;
            Q30=makeQuery(id+"F0.imprint","IMPRINT",FACE,{"disambiguationData":[TD([[makeQuery(id+"F0.imprint","IMPRINT",EDGE,{"derivedFrom":sQuery(id+"F0.wireOp",EDGE,"E79.MirrorCS")}),1.0]])]});
            var Q31;
            {var subQ5=sQuery(id+"F0.wireOp",EDGE,"2LPYm9Wn-qhFc-XUaE-MPA3-gi2jofKje79Q.top");Q31=makeQuery(id+"F0.imprint","IMPRINT",FACE,{"disambiguationData":[TD([[makeQuery(id+"F0.imprint","IMPRINT",EDGE,{"derivedFrom":subQ5}),-1.0]])]});}
            var Q32;
            Q32=makeQuery(id+"F0.imprint","IMPRINT",FACE,{"disambiguationData":[TD([[makeQuery(id+"F0.imprint","IMPRINT",EDGE,{"derivedFrom":sQuery(id+"F0.wireOp",EDGE,"E7.left")}),1.0]])]});
            var Q33;
            Q33=makeQuery(id+"F0.imprint","IMPRINT",FACE,{"disambiguationData":[TD([[makeQuery(id+"F0.imprint","IMPRINT",EDGE,{"derivedFrom":sQuery(id+"F0.wireOp",EDGE,"E46")}),1.0]])]});
            var Q34;
            Q34=makeQuery(id+"F0.imprint","IMPRINT",FACE,{"disambiguationData":[TD([[makeQuery(id+"F0.imprint","IMPRINT",EDGE,{"derivedFrom":sQuery(id+"F0.wireOp",EDGE,"E47.MirrorC")}),-1.0]])]});
            var Q35;
            {var subQ0=sQuery(id+"F0.wireOp",EDGE,"E91.top");Q35=makeQuery(id+"F0.imprint","IMPRINT",FACE,{"disambiguationData":[TD([[makeQuery(id+"F0.imprint","IMPRINT",EDGE,{"derivedFrom":subQ0}),-1.0]])]});}
            var Q36;
            {var subQ0=sQuery(id+"F0.wireOp",EDGE,"E91.bottom");Q36=makeQuery(id+"F0.imprint","IMPRINT",FACE,{"disambiguationData":[TD([[makeQuery(id+"F0.imprint","IMPRINT",EDGE,{"derivedFrom":subQ0}),1.0]])]});}
            var Q37;
            {var subQ15=sQuery(id+"F0.wireOp",EDGE,"E74.bottom");Q37=makeQuery(id+"F0.imprint","IMPRINT",FACE,{"disambiguationData":[TD([[makeQuery(id+"F0.imprint","IMPRINT",EDGE,{"derivedFrom":subQ15}),-1.0]])]});}
            extrude(context, id + "F1", {"entities" : qUnion([Q0, Q1, Q2, Q3, Q4, Q5, Q6, Q7, Q8, Q9, Q10, Q11, Q12, Q13, Q14, Q15, Q16, Q17, Q18, Q19, Q20, Q21, Q22, Q23, Q24, Q25, Q26, Q27, Q28, Q29, Q30, Q31, Q32, Q33, Q34, Q35, Q36, Q37]), "depth" : 6.35 * mm, "offsetDistance" : 25.4 * mm});
        }
        {
            var Q0;
            Q0=sQuery(id+"F0.wireOp",VERTEX,"E48.center");
            var Q1;
            Q1=sQuery(id+"F0.wireOp",VERTEX,"E49.MirrorC.center");
            var Q2;
            Q2=sQuery(id+"F0.wireOp",VERTEX,"E51.MirrorC.center");
            var Q3;
            Q3=sQuery(id+"F0.wireOp",VERTEX,"E50.MirrorC.center");
            var Q4;
            Q4=makeQuery(id+"F1.opExtrude","SWEPT_BODY",BODY,{"disambiguationData":[OSD([sQuery(id+"F0.wireOp",EDGE,"E7.left"),sQuery(id+"F0.wireOp",EDGE,"E8.bottom"),sQuery(id+"F0.wireOp",EDGE,"E8.top"),sQuery(id+"F0.wireOp",EDGE,"E8.left"),sQuery(id+"F0.wireOp",EDGE,"E8.right"),sQuery(id+"F0.wireOp",EDGE,"E10.MirrorCS"),sQuery(id+"F0.wireOp",EDGE,"E11.MirrorCS"),sQuery(id+"F0.wireOp",EDGE,"E13.MirrorCS"),sQuery(id+"F0.wireOp",EDGE,"E14.MirrorCS"),sQuery(id+"F0.wireOp",EDGE,"E36.bottom"),sQuery(id+"F0.wireOp",EDGE,"E36.top"),sQuery(id+"F0.wireOp",EDGE,"E38.left"),sQuery(id+"F0.wireOp",EDGE,"E38.right"),sQuery(id+"F0.wireOp",EDGE,"E39.0"),sQuery(id+"F0.wireOp",EDGE,"E39.1"),sQuery(id+"F0.wireOp",EDGE,"E40"),sQuery(id+"F0.wireOp",EDGE,"E41"),sQuery(id+"F0.wireOp",EDGE,"E42.MirrorCS"),sQuery(id+"F0.wireOp",EDGE,"E43.MirrorCS"),sQuery(id+"F0.wireOp",EDGE,"E44.MirrorCS"),sQuery(id+"F0.wireOp",EDGE,"E45.MirrorCS")])]});
            hole(context, id + "F2", {"style" : HoleStyle.SIMPLE, "endStyle" : HoleEndStyle.THROUGH, "oppositeDirection" : true, "standardTappedOrClearance" : lookupTablePath({ "standard" : "ANSI", "engagement" : "75%", "pitch" : "32 tpi", "size" : "#6", "type" : "Tapped" }), "standardBlindInLast" : lookupTablePath({ "standard" : "ANSI", "engagement" : "75%", "pitch" : "32 tpi", "size" : "#6", "type" : "Tapped" }), "holeDiameter" : 2.7 * mm, "majorDiameter" : 3.5 * mm, "showTappedDepth" : true, "isTappedThrough" : true, "tappedDepth" : 12.7 * mm, "tapClearance" : 3, "locations" : qUnion([Q0, Q1, Q2, Q3]), "scope" : qUnion([Q4])});
        }
        {
            var Q0;
            Q0=sQuery(id+"F0.wireOp",VERTEX,"E46.center");
            var Q1;
            Q1=sQuery(id+"F0.wireOp",VERTEX,"E47.MirrorC.center");
            var Q2;
            Q2=makeQuery(id+"F1.opExtrude","SWEPT_BODY",BODY,{"disambiguationData":[OSD([sQuery(id+"F0.wireOp",EDGE,"E7.left"),sQuery(id+"F0.wireOp",EDGE,"E8.bottom"),sQuery(id+"F0.wireOp",EDGE,"E8.top"),sQuery(id+"F0.wireOp",EDGE,"E8.left"),sQuery(id+"F0.wireOp",EDGE,"E8.right"),sQuery(id+"F0.wireOp",EDGE,"E10.MirrorCS"),sQuery(id+"F0.wireOp",EDGE,"E11.MirrorCS"),sQuery(id+"F0.wireOp",EDGE,"E13.MirrorCS"),sQuery(id+"F0.wireOp",EDGE,"E14.MirrorCS"),sQuery(id+"F0.wireOp",EDGE,"E36.bottom"),sQuery(id+"F0.wireOp",EDGE,"E36.top"),sQuery(id+"F0.wireOp",EDGE,"E38.left"),sQuery(id+"F0.wireOp",EDGE,"E38.right"),sQuery(id+"F0.wireOp",EDGE,"E39.0"),sQuery(id+"F0.wireOp",EDGE,"E39.1"),sQuery(id+"F0.wireOp",EDGE,"E40"),sQuery(id+"F0.wireOp",EDGE,"E41"),sQuery(id+"F0.wireOp",EDGE,"E42.MirrorCS"),sQuery(id+"F0.wireOp",EDGE,"E43.MirrorCS"),sQuery(id+"F0.wireOp",EDGE,"E44.MirrorCS"),sQuery(id+"F0.wireOp",EDGE,"E45.MirrorCS")])]});
            hole(context, id + "F3", {"style" : HoleStyle.SIMPLE, "endStyle" : HoleEndStyle.THROUGH, "oppositeDirection" : true, "standardTappedOrClearance" : lookupTablePath({ "standard" : "ANSI", "engagement" : "75%", "pitch" : "20 tpi", "size" : "1/4", "type" : "Tapped" }), "standardBlindInLast" : lookupTablePath({ "standard" : "ANSI", "engagement" : "75%", "pitch" : "20 tpi", "size" : "1/4", "type" : "Tapped" }), "holeDiameter" : 5.1 * mm, "majorDiameter" : 6.35 * mm, "showTappedDepth" : true, "isTappedThrough" : true, "tappedDepth" : 12.7 * mm, "tapClearance" : 3, "locations" : qUnion([Q0, Q1]), "scope" : qUnion([Q2])});
        }
        {
            var Q0;
            Q0=sQuery(id+"F0.wireOp",VERTEX,"E52.center");
            var Q1;
            Q1=sQuery(id+"F0.wireOp",VERTEX,"E53.center");
            var Q2;
            Q2=sQuery(id+"F0.wireOp",VERTEX,"fdd06f5c-8cbb-4d59-a9f2-426be867a0200.MirrorC.center");
            var Q3;
            Q3=sQuery(id+"F0.wireOp",VERTEX,"E54.MirrorC.center");
            var Q4;
            Q4=makeQuery(id+"F1.opExtrude","SWEPT_BODY",BODY,{"disambiguationData":[OSD([sQuery(id+"F0.wireOp",EDGE,"E0.top"),sQuery(id+"F0.wireOp",EDGE,"E0.left"),sQuery(id+"F0.wireOp",EDGE,"E0.right"),sQuery(id+"F0.wireOp",EDGE,"E1.0"),sQuery(id+"F0.wireOp",EDGE,"E2.0"),sQuery(id+"F0.wireOp",EDGE,"E5.MirrorCS"),sQuery(id+"F0.wireOp",EDGE,"E6.0"),sQuery(id+"F0.wireOp",EDGE,"E15"),sQuery(id+"F0.wireOp",EDGE,"E16"),sQuery(id+"F0.wireOp",EDGE,"E17.1.0"),sQuery(id+"F0.wireOp",EDGE,"E17.2.0"),sQuery(id+"F0.wireOp",EDGE,"E17.3.0"),sQuery(id+"F0.wireOp",EDGE,"E18.MirrorC"),sQuery(id+"F0.wireOp",EDGE,"E19.MirrorC"),sQuery(id+"F0.wireOp",EDGE,"E20.MirrorC"),sQuery(id+"F0.wireOp",EDGE,"E22.MirrorC"),sQuery(id+"F0.wireOp",EDGE,"E23.MirrorC"),sQuery(id+"F0.wireOp",EDGE,"E25"),sQuery(id+"F0.wireOp",EDGE,"E26.MirrorC"),sQuery(id+"F0.wireOp",EDGE,"E27.top"),sQuery(id+"F0.wireOp",EDGE,"E27.left"),sQuery(id+"F0.wireOp",EDGE,"E27.right"),sQuery(id+"F0.wireOp",EDGE,"E29.MirrorCS"),sQuery(id+"F0.wireOp",EDGE,"E30.MirrorC"),sQuery(id+"F0.wireOp",EDGE,"E31.MirrorC"),sQuery(id+"F0.wireOp",EDGE,"E34.MirrorCS"),sQuery(id+"F0.wireOp",EDGE,"E35.MirrorCS"),sQuery(id+"F0.wireOp",EDGE,"1ff027d5-e3b4-4671-8476-58aee43777f90.MirrorC"),sQuery(id+"F0.wireOp",EDGE,"1ff027d5-e3b4-4671-8476-58aee43777f91.MirrorCS"),sQuery(id+"F0.wireOp",EDGE,"1ff027d5-e3b4-4671-8476-58aee43777f93.MirrorC"),sQuery(id+"F0.wireOp",EDGE,"1ff027d5-e3b4-4671-8476-58aee43777f94.MirrorCS"),sQuery(id+"F0.wireOp",EDGE,"1ff027d5-e3b4-4671-8476-58aee43777f95.MirrorC"),sQuery(id+"F0.wireOp",EDGE,"1ff027d5-e3b4-4671-8476-58aee43777f96.MirrorCS"),sQuery(id+"F0.wireOp",EDGE,"1ff027d5-e3b4-4671-8476-58aee43777f97.MirrorC"),sQuery(id+"F0.wireOp",EDGE,"1ff027d5-e3b4-4671-8476-58aee43777f912.MirrorCS"),sQuery(id+"F0.wireOp",EDGE,"1ff027d5-e3b4-4671-8476-58aee43777f913.MirrorCS"),sQuery(id+"F0.wireOp",EDGE,"1ff027d5-e3b4-4671-8476-58aee43777f914.MirrorCS"),sQuery(id+"F0.wireOp",EDGE,"E55.0"),sQuery(id+"F0.wireOp",EDGE,"E56"),sQuery(id+"F0.wireOp",EDGE,"E57")])]});
            hole(context, id + "F4", {"style" : HoleStyle.SIMPLE, "endStyle" : HoleEndStyle.THROUGH, "oppositeDirection" : true, "standardTappedOrClearance" : lookupTablePath({ "standard" : "ANSI", "engagement" : "75%", "pitch" : "20 tpi", "size" : "1/4", "type" : "Tapped" }), "standardBlindInLast" : lookupTablePath({ "standard" : "ANSI", "engagement" : "75%", "pitch" : "20 tpi", "size" : "1/4", "type" : "Tapped" }), "holeDiameter" : 5.1 * mm, "majorDiameter" : 6.35 * mm, "showTappedDepth" : true, "isTappedThrough" : true, "tappedDepth" : 12.7 * mm, "tapClearance" : 3, "locations" : qUnion([Q0, Q1, Q2, Q3]), "scope" : qUnion([Q4])});
        }
    });
